# Revit family: RWL2
name_source: partatom
category: Lighting Fixtures
revit_build: Autodesk Revit 2014 (Build: 20130308_1515(x64)
units: mm (PartAtom-declared; Revit-internal decimal feet)

## types (1)
- RWL2
    Apparent Load = 109 VA
    Assembly Code = D5020200
    Color Filter = 16777215
    Default Elevation = 48 "
    Description = RWL2 Ratio
    Dimming Lamp Color Temperature Shift = <None>
    Features = Mid-size for mounting heights up to 25ft and spacing up to 100ft
Featuring Micro Strike Optics which maximizes target zone illumination with minimal losses at the house-side,reducing light trespass issues.
Visual comfort standard
Micro Strike optics in Type 2, 3, and 4W distributions
Matching rectilinear form to the Ratio Family
Versatile mounting for multiple lighting applications
Large variety of wattages to target specific lumen outputs
Control options including photo control, occupancy sensing,NX Distributed Intelligence™ and 7-Pin with networked controls
    Housing = Paint - Hubbell - Textured Camera Black
    Lamp = LED Lamp
    Load Classification = Lighting
    Manufacturer = Hubbell Outdoor Lighting
    Material Finish = Paint  - Hubbell - White
    Model = RWL2
    Opal lens = Hubbell - White Glass
    Photometric Note = For more Photometrics Please vist above Link
    Photometric Web File = RWL2-160L-115-3K7-2.ies
    Photometric Web Link = https://www.hubbell.com
    Power Factor = 1
    Product Documentation Link = https://hubbellcdn.com
    Product Page URL = https://www.hubbell.com
    Tilt Angle = 60.00°
    URL = https://www.hubbell.com
    Voltage = 120 V
    Warranty = Five year warranty
    Wattage Comments = 46W to 157W
    Watts = 109 W
    zz Length 1 = 23.7 "
    zz Length 2 = 23.7 "

## geometry (parser evidence)
native form markers: Sweep x3
no freeform markers — native parametric forms only
